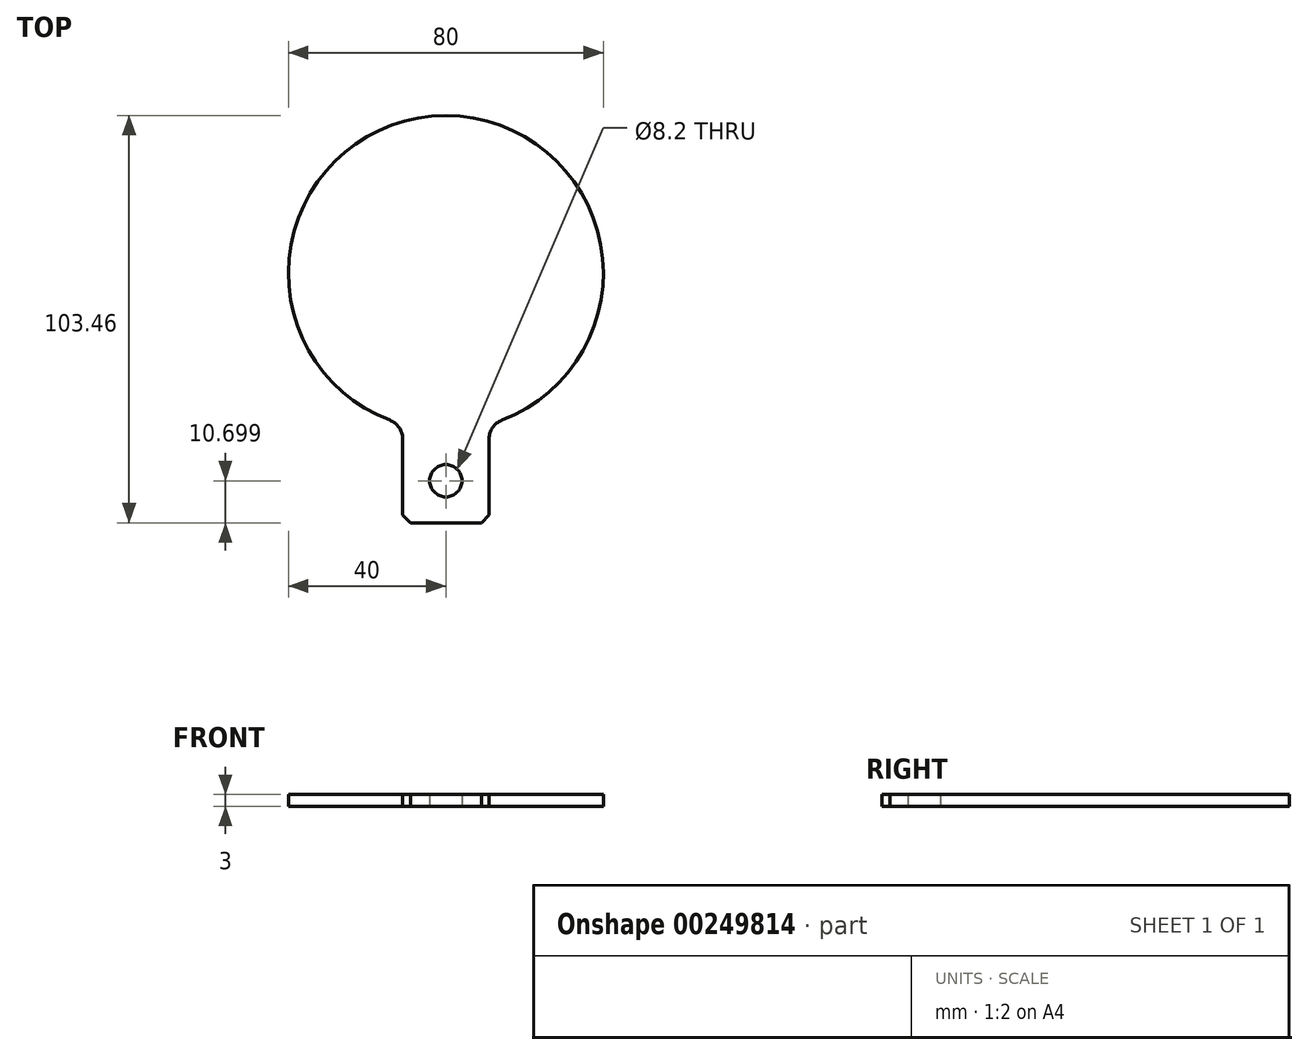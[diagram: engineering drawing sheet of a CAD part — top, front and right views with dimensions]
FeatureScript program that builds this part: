
annotation { "Feature Type Name" : "Feature", "Feature Type Description" : "" }
export const myFeature = defineFeature(function(context is Context, id is Id, definition is map)
    precondition{}
    {
        {
            var Q0;
            Q0=qCreatedBy(makeId("Top.planeOp"),FACE);
            var sketch = newSketch(context, id + "F0", { "sketchPlane" : qUnion([Q0])});
            skLineSegment(sketch, "E0.top", {"start": v(-11, -25) * mm, "end": v(11, -25) * mm});
            skLineSegment(sketch, "E0.left", {"start": v(-11, -3.6) * mm, "end": v(-11, -25) * mm});
            skLineSegment(sketch, "E0.right", {"start": v(11, -3.6) * mm, "end": v(11, -25) * mm});
            skArc(sketch, "E1", {"start": v(14.22, 1.07) * mm, "mid": v(0, 78.46) * mm, "end": v(-14.22, 1.07) * mm});
            skPoint(sketch, "E2.visualSharp", {"position": v(-11, 0) * mm});
            skArc(sketch, "E2.filletArc", {"start": v(-11, -3.6) * mm, "mid": v(-11.88, -0.76) * mm, "end": v(-14.22, 1.07) * mm});
            skPoint(sketch, "E3.visualSharp", {"position": v(11, 0) * mm});
            skArc(sketch, "E3.filletArc", {"start": v(14.22, 1.07) * mm, "mid": v(11.88, -0.76) * mm, "end": v(11, -3.6) * mm});
            skCircle(sketch, "E4", {"center": v(0, -14.3) * mm, "radius": 4.1 * mm});
            skPoint(sketch, "E4.centerSnap0", {"position": v(-11, -14.3) * mm});
            skSolve(sketch);
        }
        {
            var Q0;
            Q0 = qSketchRegion(id + "F0", true);
            extrude(context, id + "F1", {"entities" : qUnion([Q0]), "depth" : 3 * mm});
        }
        {
            var Q0;
            Q0=makeQuery(id+"F1.opExtrude","SWEPT_EDGE",EDGE,{"disambiguationData":[OSD([sQuery(id+"F0.wireOp",EDGE,"E0.top"),sQuery(id+"F0.wireOp",EDGE,"E0.right")])]});
            var Q1;
            Q1=makeQuery(id+"F1.opExtrude","SWEPT_EDGE",EDGE,{"disambiguationData":[OSD([sQuery(id+"F0.wireOp",EDGE,"E0.top"),sQuery(id+"F0.wireOp",EDGE,"E0.left")])]});
            chamfer(context, id + "F2", {"entities" : qUnion([Q0, Q1]), "width" : 2 * mm, "tangentPropagation" : true});
        }
    });
